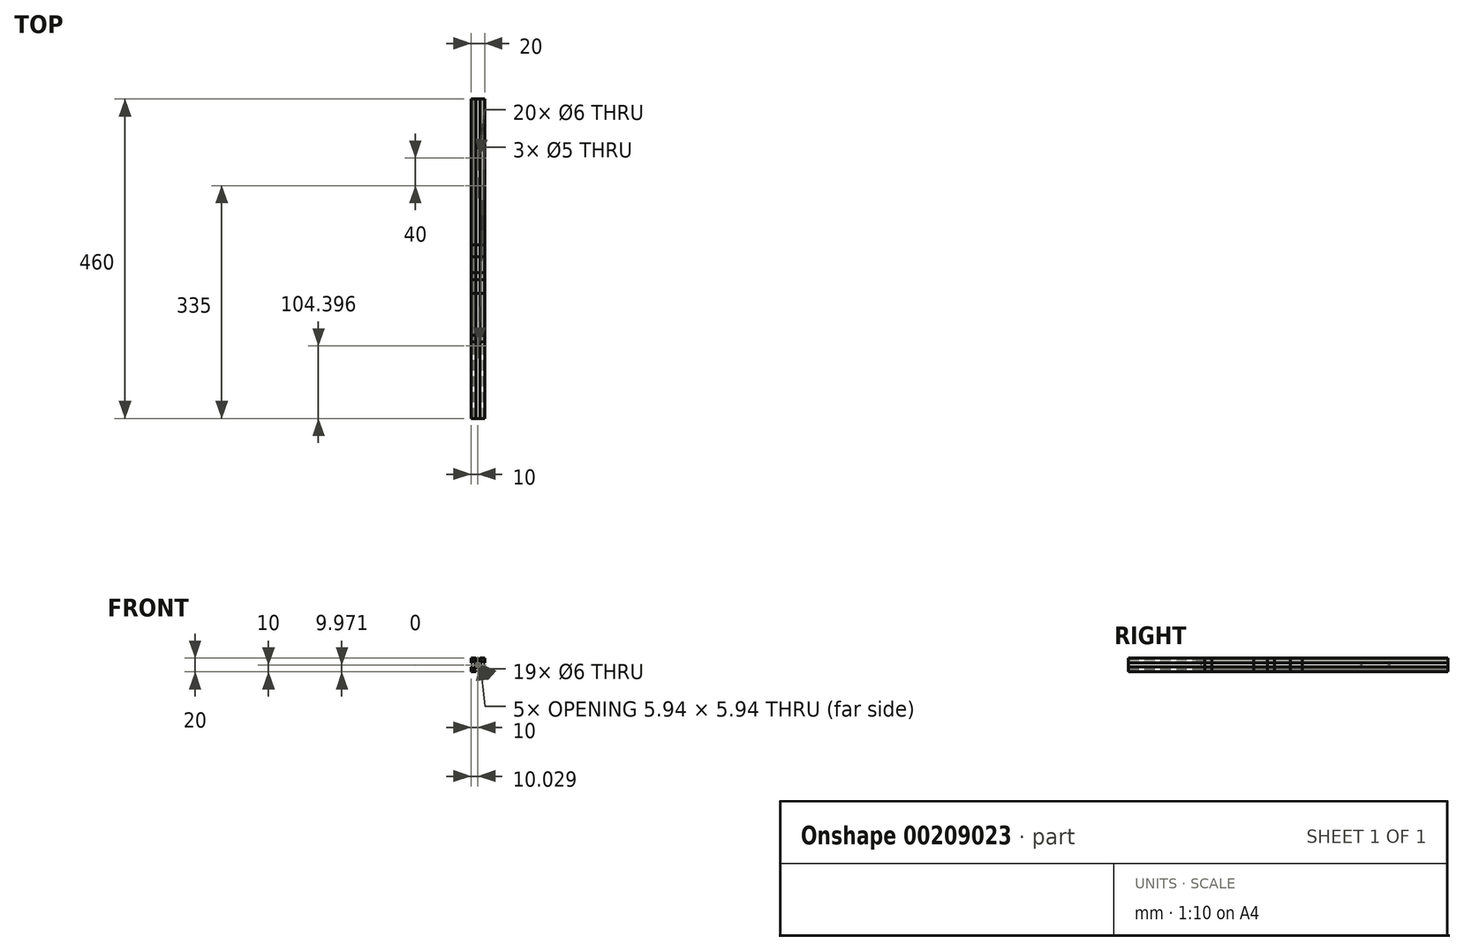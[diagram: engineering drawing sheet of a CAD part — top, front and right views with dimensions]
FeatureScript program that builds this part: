
annotation { "Feature Type Name" : "Feature", "Feature Type Description" : "" }
export const myFeature = defineFeature(function(context is Context, id is Id, definition is map)
    precondition{}
    {
        {
            var Q0;
            Q0=qCreatedBy(makeId("Front.planeOp"),FACE);
            var sketch = newSketch(context, id + "F0", { "sketchPlane" : qUnion([Q0])});
            skCircle(sketch, "E0", {"center": v(0, 0) * mm, "radius": 3 * mm});
            skLineSegment(sketch, "E1.left", {"start": v(3, 8) * mm, "end": v(3, 10) * mm});
            skLineSegment(sketch, "E2", {"start": v(3, 10) * mm, "end": v(10, 10) * mm});
            skLineSegment(sketch, "E3", {"start": v(3, 8) * mm, "end": v(5.19, 8) * mm});
            skLineSegment(sketch, "E4", {"start": v(0, 4) * mm, "end": v(1.21, 4) * mm});
            skLineSegment(sketch, "E5", {"start": v(0, 0) * mm, "end": v(10, 10) * mm, "construction": true});
            skArc(sketch, "E6", {"start": v(1.21, 4) * mm, "mid": v(4.03, 5.17) * mm, "end": v(5.19, 8) * mm});
            skLineSegment(sketch, "E7.MirrorCS", {"start": v(10, 3) * mm, "end": v(10, 10) * mm});
            skLineSegment(sketch, "E8.MirrorCS", {"start": v(8, 3) * mm, "end": v(10, 3) * mm});
            skLineSegment(sketch, "E9.MirrorCS", {"start": v(8, 3) * mm, "end": v(8, 5.19) * mm});
            skArc(sketch, "E10.MirrorCS", {"start": v(4, 1.21) * mm, "mid": v(5.17, 4.03) * mm, "end": v(8, 5.19) * mm});
            skLineSegment(sketch, "E11.MirrorCS", {"start": v(4, 0) * mm, "end": v(4, 1.21) * mm});
            skLineSegment(sketch, "E12.MirrorCS", {"start": v(-3, 8) * mm, "end": v(-3, 10) * mm});
            skLineSegment(sketch, "E13.MirrorCS", {"start": v(-3, 10) * mm, "end": v(-10, 10) * mm});
            skArc(sketch, "E14.MirrorCS", {"start": v(-4, 1.21) * mm, "mid": v(-5.17, 4.03) * mm, "end": v(-8, 5.19) * mm});
            skLineSegment(sketch, "E15.MirrorCS", {"start": v(-4, 0) * mm, "end": v(-4, 1.21) * mm});
            skLineSegment(sketch, "E16.MirrorCS", {"start": v(0, 4) * mm, "end": v(-1.21, 4) * mm});
            skLineSegment(sketch, "E17.MirrorCS", {"start": v(0, 0) * mm, "end": v(-10, 10) * mm, "construction": true});
            skLineSegment(sketch, "E18.MirrorCS", {"start": v(-8, 3) * mm, "end": v(-10, 3) * mm});
            skLineSegment(sketch, "E19.MirrorCS", {"start": v(-8, 3) * mm, "end": v(-8, 5.19) * mm});
            skLineSegment(sketch, "E20.MirrorCS", {"start": v(-10, 3) * mm, "end": v(-10, 10) * mm});
            skLineSegment(sketch, "E21.MirrorCS", {"start": v(-3, 8) * mm, "end": v(-5.19, 8) * mm});
            skArc(sketch, "E22.MirrorCS", {"start": v(-1.21, 4) * mm, "mid": v(-4.03, 5.17) * mm, "end": v(-5.19, 8) * mm});
            skLineSegment(sketch, "E23.MirrorCS", {"start": v(0, -4) * mm, "end": v(-1.21, -4) * mm});
            skLineSegment(sketch, "E24.MirrorCS", {"start": v(-8, -3) * mm, "end": v(-10, -3) * mm});
            skLineSegment(sketch, "E25.MirrorCS", {"start": v(-10, -3) * mm, "end": v(-10, -10) * mm});
            skArc(sketch, "E26.MirrorCS", {"start": v(-1.21, -4) * mm, "mid": v(-4.03, -5.17) * mm, "end": v(-5.19, -8) * mm});
            skLineSegment(sketch, "E27.MirrorCS", {"start": v(-3, -8) * mm, "end": v(-3, -10) * mm});
            skLineSegment(sketch, "E28.MirrorCS", {"start": v(4, 0) * mm, "end": v(4, -1.21) * mm});
            skArc(sketch, "E29.MirrorCS", {"start": v(4, -1.21) * mm, "mid": v(5.17, -4.03) * mm, "end": v(8, -5.19) * mm});
            skLineSegment(sketch, "E30.MirrorCS", {"start": v(8, -3) * mm, "end": v(8, -5.19) * mm});
            skLineSegment(sketch, "E31.MirrorCS", {"start": v(8, -3) * mm, "end": v(10, -3) * mm});
            skLineSegment(sketch, "E32.MirrorCS", {"start": v(10, -3) * mm, "end": v(10, -10) * mm});
            skArc(sketch, "E33.MirrorCS", {"start": v(1.21, -4) * mm, "mid": v(4.03, -5.17) * mm, "end": v(5.19, -8) * mm});
            skLineSegment(sketch, "E34.MirrorCS", {"start": v(0, 0) * mm, "end": v(10, -10) * mm, "construction": true});
            skLineSegment(sketch, "E35.MirrorCS", {"start": v(0, -4) * mm, "end": v(1.21, -4) * mm});
            skLineSegment(sketch, "E36.MirrorCS", {"start": v(3, -8) * mm, "end": v(5.19, -8) * mm});
            skLineSegment(sketch, "E37.MirrorCS", {"start": v(3, -8) * mm, "end": v(3, -10) * mm});
            skLineSegment(sketch, "E38.MirrorCS", {"start": v(0, 0) * mm, "end": v(-10, -10) * mm, "construction": true});
            skArc(sketch, "E39.MirrorCS", {"start": v(-4, -1.21) * mm, "mid": v(-5.17, -4.03) * mm, "end": v(-8, -5.19) * mm});
            skLineSegment(sketch, "E40.MirrorCS", {"start": v(-3, -10) * mm, "end": v(-10, -10) * mm});
            skLineSegment(sketch, "E41.MirrorCS", {"start": v(3, -10) * mm, "end": v(10, -10) * mm});
            skLineSegment(sketch, "E42.MirrorCS", {"start": v(-3, -8) * mm, "end": v(-5.19, -8) * mm});
            skLineSegment(sketch, "E43.MirrorCS", {"start": v(-4, 0) * mm, "end": v(-4, -1.21) * mm});
            skLineSegment(sketch, "E44.MirrorCS", {"start": v(-8, -3) * mm, "end": v(-8, -5.19) * mm});
            skSolve(sketch);
        }
        {
            var Q0;
            Q0=makeQuery(id+"F0.imprint","IMPRINT",FACE,{"disambiguationData":[TD([[makeQuery(id+"F0.imprint","IMPRINT",EDGE,{"derivedFrom":sQuery(id+"F0.wireOp",EDGE,"E0")}),-1.0]])]});
            extrude(context, id + "F1", {"entities" : qUnion([Q0]), "depth" : 350 * mm});
        }
        {
            var Q0;
            Q0=qSketchRegion(id+"F0",true);
            extrude(context, id + "F2", {"entities" : qUnion([Q0]), "depth" : 260 * mm});
        }
        {
            var Q0;
            Q0=qSketchRegion(id+"F0",true);
            extrude(context, id + "F3", {"entities" : qUnion([Q0]), "depth" : 460 * mm});
        }
        {
            var Q0;
            Q0=qSketchRegion(id+"F0",true);
            extrude(context, id + "F4", {"entities" : qUnion([Q0]), "depth" : 280 * mm});
        }
        {
            var Q0;
            Q0=qSketchRegion(id+"F0",true);
            extrude(context, id + "F5", {"entities" : qUnion([Q0]), "depth" : 210 * mm});
        }
        {
            var Q0;
            Q0=makeQuery(id+"F5.opExtrude","SWEPT_FACE",FACE,{"disambiguationData":[OSD([sQuery(id+"F0.wireOp",EDGE,"E2")])]});
            var sketch = newSketch(context, id + "F6", { "sketchPlane" : qUnion([Q0])});
            skLineSegment(sketch, "E45", {"start": v(0, -105) * mm, "end": v(10, -105) * mm, "construction": true});
            skLineSegment(sketch, "E46", {"start": v(0, -105) * mm, "end": v(0, 26.92) * mm, "construction": true});
            skCircle(sketch, "E47", {"center": v(0, -85) * mm, "radius": 3 * mm});
            skCircle(sketch, "E48.MirrorC", {"center": v(0, -125) * mm, "radius": 3 * mm});
            skSolve(sketch);
        }
        {
            var Q0;
            Q0=qSketchRegion(id+"F6",true);
            extrude(context, id + "F7", {"entities" : qUnion([Q0]), "operationType" : NewBodyOperationType.REMOVE, "endBound" : BoundingType.THROUGH_ALL, "oppositeDirection" : true, "depth" : 25 * mm});
        }
        {
            var Q0;
            Q0=qSketchRegion(id+"F0",true);
            extrude(context, id + "F8", {"entities" : qUnion([Q0]), "depth" : 250 * mm});
        }
        {
            var Q0;
            Q0=makeQuery(id+"F1.opExtrude","CAP_FACE",FACE,{"disambiguationData":[OSD([sQuery(id+"F0.wireOp",EDGE,"E0"),sQuery(id+"F0.wireOp",EDGE,"E1.left"),sQuery(id+"F0.wireOp",EDGE,"E2"),sQuery(id+"F0.wireOp",EDGE,"E3"),sQuery(id+"F0.wireOp",EDGE,"E4"),sQuery(id+"F0.wireOp",EDGE,"E6"),sQuery(id+"F0.wireOp",EDGE,"E7.MirrorCS"),sQuery(id+"F0.wireOp",EDGE,"E8.MirrorCS"),sQuery(id+"F0.wireOp",EDGE,"E9.MirrorCS"),sQuery(id+"F0.wireOp",EDGE,"E10.MirrorCS"),sQuery(id+"F0.wireOp",EDGE,"E11.MirrorCS"),sQuery(id+"F0.wireOp",EDGE,"E12.MirrorCS"),sQuery(id+"F0.wireOp",EDGE,"E13.MirrorCS"),sQuery(id+"F0.wireOp",EDGE,"E14.MirrorCS"),sQuery(id+"F0.wireOp",EDGE,"E15.MirrorCS"),sQuery(id+"F0.wireOp",EDGE,"E16.MirrorCS"),sQuery(id+"F0.wireOp",EDGE,"E18.MirrorCS"),sQuery(id+"F0.wireOp",EDGE,"E19.MirrorCS"),sQuery(id+"F0.wireOp",EDGE,"E20.MirrorCS"),sQuery(id+"F0.wireOp",EDGE,"E21.MirrorCS"),sQuery(id+"F0.wireOp",EDGE,"E22.MirrorCS"),sQuery(id+"F0.wireOp",EDGE,"E23.MirrorCS"),sQuery(id+"F0.wireOp",EDGE,"E24.MirrorCS"),sQuery(id+"F0.wireOp",EDGE,"E25.MirrorCS"),sQuery(id+"F0.wireOp",EDGE,"E26.MirrorCS"),sQuery(id+"F0.wireOp",EDGE,"E27.MirrorCS"),sQuery(id+"F0.wireOp",EDGE,"E28.MirrorCS"),sQuery(id+"F0.wireOp",EDGE,"E29.MirrorCS"),sQuery(id+"F0.wireOp",EDGE,"E30.MirrorCS"),sQuery(id+"F0.wireOp",EDGE,"E31.MirrorCS"),sQuery(id+"F0.wireOp",EDGE,"E32.MirrorCS"),sQuery(id+"F0.wireOp",EDGE,"E33.MirrorCS"),sQuery(id+"F0.wireOp",EDGE,"E35.MirrorCS"),sQuery(id+"F0.wireOp",EDGE,"E36.MirrorCS"),sQuery(id+"F0.wireOp",EDGE,"E37.MirrorCS"),sQuery(id+"F0.wireOp",EDGE,"E39.MirrorCS"),sQuery(id+"F0.wireOp",EDGE,"E40.MirrorCS"),sQuery(id+"F0.wireOp",EDGE,"E41.MirrorCS"),sQuery(id+"F0.wireOp",EDGE,"E42.MirrorCS"),sQuery(id+"F0.wireOp",EDGE,"E43.MirrorCS"),sQuery(id+"F0.wireOp",EDGE,"E44.MirrorCS")])],"isStart":false});
            var sketch = newSketch(context, id + "F9", { "sketchPlane" : qUnion([Q0])});
            skLineSegment(sketch, "E49", {"start": v(0, 8.7) * mm, "end": v(3, 8.7) * mm});
            skLineSegment(sketch, "E50", {"start": v(3, 8.7) * mm, "end": v(3, 8) * mm});
            skLineSegment(sketch, "E51", {"start": v(3, 8) * mm, "end": v(5.19, 8) * mm});
            skArc(sketch, "E52.0", {"start": v(4.65, 5.97) * mm, "mid": v(5.05, 6.95) * mm, "end": v(5.19, 8) * mm});
            skLineSegment(sketch, "E53", {"start": v(0, 5.97) * mm, "end": v(4.65, 5.97) * mm});
            skPoint(sketch, "E54.orphan", {"position": v(1.21, 4) * mm});
            skLineSegment(sketch, "E55.MirrorCS", {"start": v(0, 8.7) * mm, "end": v(-3, 8.7) * mm});
            skLineSegment(sketch, "E56.MirrorCS", {"start": v(-3, 8.7) * mm, "end": v(-3, 8) * mm});
            skLineSegment(sketch, "E57.MirrorCS", {"start": v(-3, 8) * mm, "end": v(-5.19, 8) * mm});
            skArc(sketch, "E58.MirrorCS", {"start": v(-4.65, 5.97) * mm, "mid": v(-5.05, 6.95) * mm, "end": v(-5.19, 8) * mm});
            skLineSegment(sketch, "E59.MirrorCS", {"start": v(0, 5.97) * mm, "end": v(-4.65, 5.97) * mm});
            skSolve(sketch);
        }
        {
            var Q0;
            Q0=qSketchRegion(id+"F9",true);
            extrude(context, id + "F10", {"entities" : qUnion([Q0]), "depth" : 12 * mm});
        }
        {
            var Q0;
            Q0=makeQuery(id+"F10.opExtrude","SWEPT_FACE",FACE,{"disambiguationData":[OSD([sQuery(id+"F9.wireOp",EDGE,"E49"),sQuery(id+"F9.wireOp",EDGE,"E55.MirrorCS")])]});
            var sketch = newSketch(context, id + "F11", { "sketchPlane" : qUnion([Q0])});
            skCircle(sketch, "E60", {"center": v(0, -355.6) * mm, "radius": 2.5 * mm});
            skPoint(sketch, "E60.centerSnap0", {"position": v(0, -362) * mm});
            skSolve(sketch);
        }
        {
            var Q0;
            Q0=qSketchRegion(id+"F11",true);
            extrude(context, id + "F12", {"entities" : qUnion([Q0]), "operationType" : NewBodyOperationType.REMOVE, "endBound" : BoundingType.THROUGH_ALL, "oppositeDirection" : true, "depth" : 25 * mm});
        }
        {
            var Q0;
            Q0=qSketchRegion(id+"F0",true);
            extrude(context, id + "F13", {"entities" : qUnion([Q0]), "depth" : 460 * mm});
        }
        {
            var Q0;
            Q0=qSketchRegion(id+"F0",true);
            extrude(context, id + "F14", {"entities" : qUnion([Q0]), "depth" : 227 * mm});
        }
        {
            var Q0;
            Q0=qSketchRegion(id+"F0",true);
            extrude(context, id + "F15", {"entities" : qUnion([Q0]), "depth" : 340 * mm});
        }
    });
